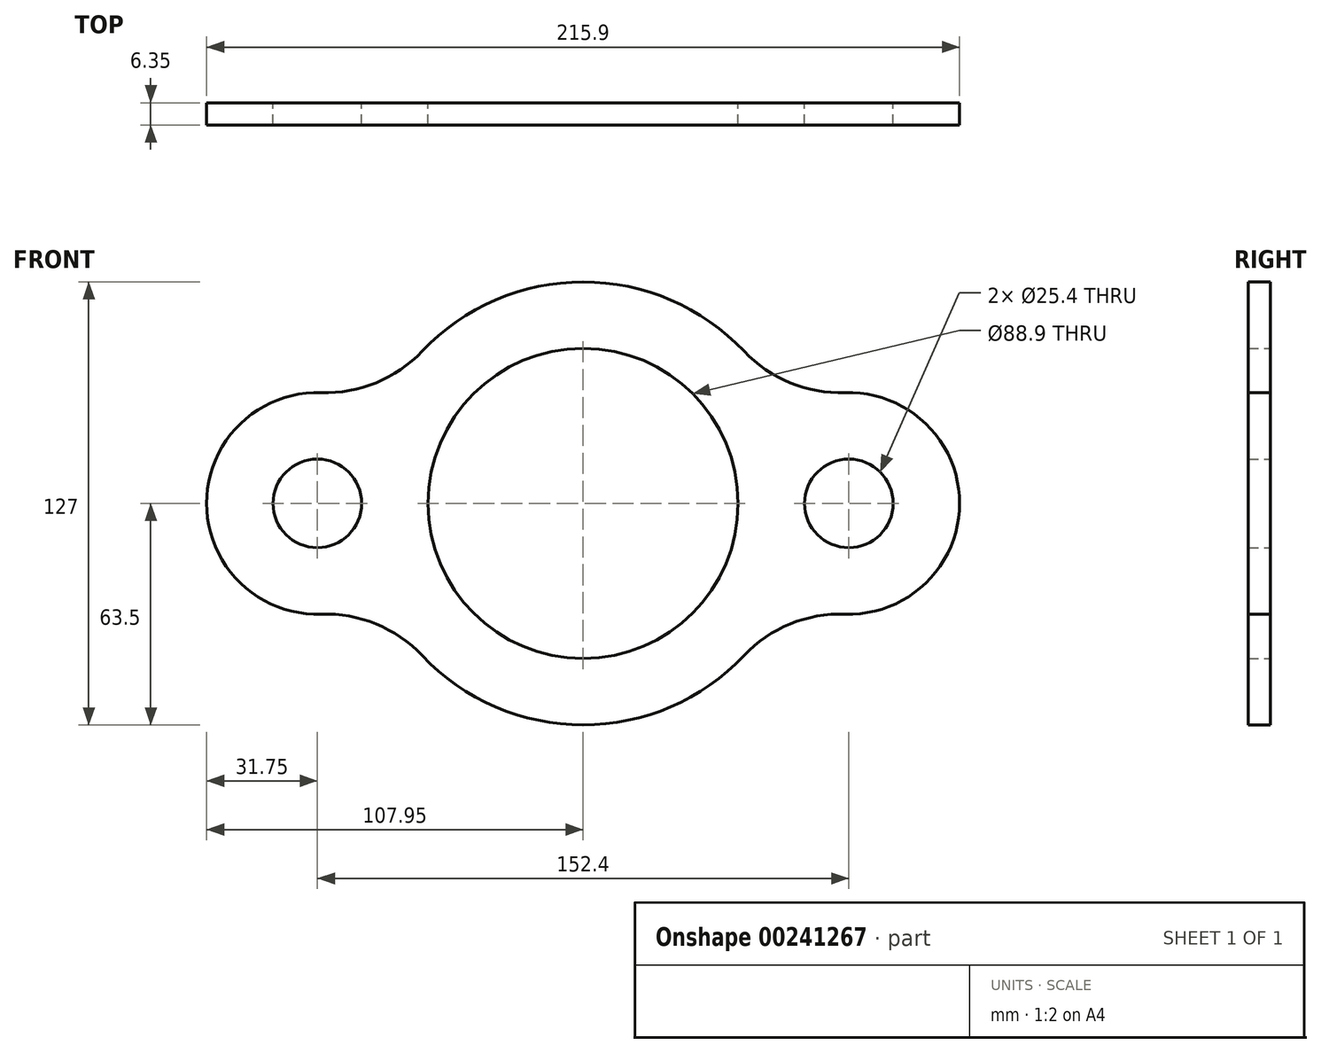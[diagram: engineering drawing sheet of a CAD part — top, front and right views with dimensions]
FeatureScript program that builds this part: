
annotation { "Feature Type Name" : "Feature", "Feature Type Description" : "" }
export const myFeature = defineFeature(function(context is Context, id is Id, definition is map)
    precondition{}
    {
        {
            var Q0;
            Q0=qCreatedBy(makeId("Front.planeOp"),FACE);
            var sketch = newSketch(context, id + "F0", { "sketchPlane" : qUnion([Q0])});
            skCircle(sketch, "E0", {"center": v(0, 0) * mm, "radius": 44.45 * mm});
            skArc(sketch, "E1", {"start": v(-46.14, -43.63) * mm, "mid": v(0, -63.5) * mm, "end": v(46.14, -43.63) * mm});
            skArc(sketch, "E2", {"start": v(75.12, -31.73) * mm, "mid": v(107.95, 0) * mm, "end": v(75.12, 31.73) * mm});
            skArc(sketch, "E3", {"start": v(-75.12, 31.73) * mm, "mid": v(-107.95, 0) * mm, "end": v(-75.12, -31.73) * mm});
            skCircle(sketch, "E4", {"center": v(-76.2, 0) * mm, "radius": 12.7 * mm});
            skCircle(sketch, "E5", {"center": v(76.2, 0) * mm, "radius": 12.7 * mm});
            skArc(sketch, "E6.trimOffspring", {"start": v(46.14, 43.63) * mm, "mid": v(0, 63.5) * mm, "end": v(-46.14, 43.63) * mm});
            skPoint(sketch, "E7.visualSharp", {"position": v(-57.94, 25.98) * mm});
            skArc(sketch, "E7.filletArc", {"start": v(-75.12, 31.73) * mm, "mid": v(-59.35, 34.56) * mm, "end": v(-46.14, 43.63) * mm});
            skPoint(sketch, "E8.visualSharp", {"position": v(-57.94, -25.98) * mm});
            skArc(sketch, "E8.filletArc", {"start": v(-46.14, -43.63) * mm, "mid": v(-59.35, -34.56) * mm, "end": v(-75.12, -31.73) * mm});
            skPoint(sketch, "E9.visualSharp", {"position": v(57.94, -25.98) * mm});
            skArc(sketch, "E9.filletArc", {"start": v(75.12, -31.73) * mm, "mid": v(59.35, -34.56) * mm, "end": v(46.14, -43.63) * mm});
            skPoint(sketch, "E10.visualSharp", {"position": v(57.94, 25.98) * mm});
            skArc(sketch, "E10.filletArc", {"start": v(46.14, 43.63) * mm, "mid": v(59.35, 34.56) * mm, "end": v(75.12, 31.73) * mm});
            skSolve(sketch);
        }
        {
            var Q0;
            Q0 = qSketchRegion(id + "F0", true);
            extrude(context, id + "F1", {"entities" : qUnion([Q0]), "depth" : 6.35 * mm});
        }
    });
